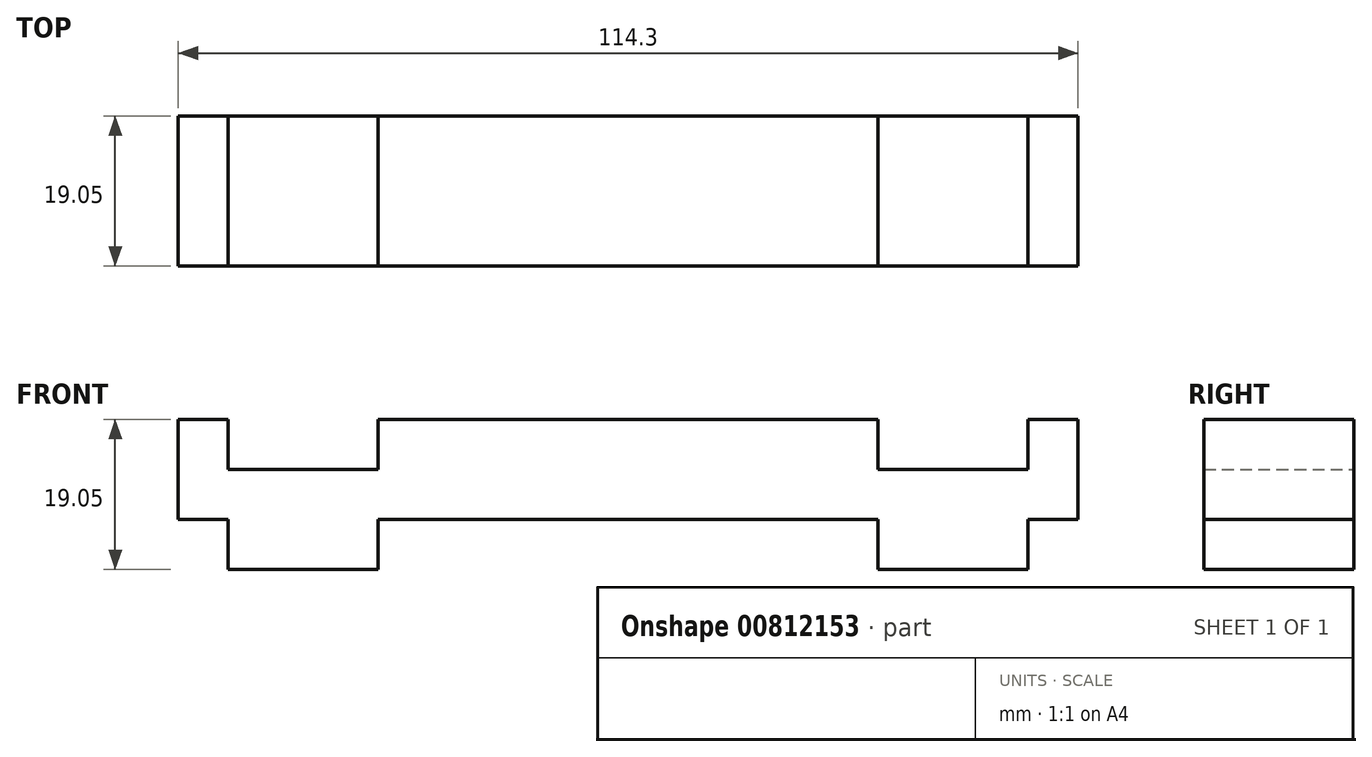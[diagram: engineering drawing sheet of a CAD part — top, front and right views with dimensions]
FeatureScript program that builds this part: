
annotation { "Feature Type Name" : "Feature", "Feature Type Description" : "" }
export const myFeature = defineFeature(function(context is Context, id is Id, definition is map)
    precondition{}
    {
        {
            var Q0;
            Q0=qCreatedBy(makeId("Front.planeOp"),FACE);
            var sketch = newSketch(context, id + "F0", { "sketchPlane" : qUnion([Q0])});
            skLineSegment(sketch, "E0", {"start": v(0, 0) * mm, "end": v(-31.75, 0) * mm});
            skLineSegment(sketch, "E1", {"start": v(-31.75, 0) * mm, "end": v(-31.75, -6.35) * mm});
            skLineSegment(sketch, "E2", {"start": v(-31.75, -6.35) * mm, "end": v(-50.8, -6.35) * mm});
            skLineSegment(sketch, "E3", {"start": v(-50.8, -6.35) * mm, "end": v(-50.8, 0) * mm});
            skLineSegment(sketch, "E4", {"start": v(-50.8, 0) * mm, "end": v(-57.15, 0) * mm});
            skLineSegment(sketch, "E5", {"start": v(-57.15, 0) * mm, "end": v(-57.15, 12.7) * mm});
            skLineSegment(sketch, "E6", {"start": v(-57.15, 12.7) * mm, "end": v(-50.8, 12.7) * mm});
            skLineSegment(sketch, "E7", {"start": v(-50.8, 12.7) * mm, "end": v(-50.8, 6.35) * mm});
            skLineSegment(sketch, "E8", {"start": v(-50.8, 6.35) * mm, "end": v(-31.75, 6.35) * mm});
            skLineSegment(sketch, "E9", {"start": v(-31.75, 6.35) * mm, "end": v(-31.75, 12.7) * mm});
            skLineSegment(sketch, "E10", {"start": v(-31.75, 12.7) * mm, "end": v(0, 12.7) * mm});
            skLineSegment(sketch, "E11.MirrorCS", {"start": v(0, 0) * mm, "end": v(31.75, 0) * mm});
            skLineSegment(sketch, "E12.MirrorCS", {"start": v(31.75, 0) * mm, "end": v(31.75, -6.35) * mm});
            skLineSegment(sketch, "E13.MirrorCS", {"start": v(31.75, 12.7) * mm, "end": v(0, 12.7) * mm});
            skLineSegment(sketch, "E14.MirrorCS", {"start": v(31.75, -6.35) * mm, "end": v(50.8, -6.35) * mm});
            skLineSegment(sketch, "E15.MirrorCS", {"start": v(50.8, 12.7) * mm, "end": v(50.8, 6.35) * mm});
            skLineSegment(sketch, "E16.MirrorCS", {"start": v(57.15, 12.7) * mm, "end": v(50.8, 12.7) * mm});
            skLineSegment(sketch, "E17.MirrorCS", {"start": v(50.8, -6.35) * mm, "end": v(50.8, 0) * mm});
            skLineSegment(sketch, "E18.MirrorCS", {"start": v(50.8, 6.35) * mm, "end": v(31.75, 6.35) * mm});
            skLineSegment(sketch, "E19.MirrorCS", {"start": v(50.8, 0) * mm, "end": v(57.15, 0) * mm});
            skLineSegment(sketch, "E20.MirrorCS", {"start": v(31.75, 6.35) * mm, "end": v(31.75, 12.7) * mm});
            skLineSegment(sketch, "E21.MirrorCS", {"start": v(57.15, 0) * mm, "end": v(57.15, 12.7) * mm});
            skSolve(sketch);
        }
        {
            var Q0;
            Q0=makeQuery(id+"F0.imprint","IMPRINT",FACE,{"disambiguationData":[TD([[makeQuery(id+"F0.imprint","IMPRINT",EDGE,{"derivedFrom":sQuery(id+"F0.wireOp",EDGE,"E0")}),-1.0]])]});
            extrude(context, id + "F1", {"entities" : qUnion([Q0]), "depth" : 19.05 * mm, "offsetDistance" : 25.4 * mm});
        }
    });
